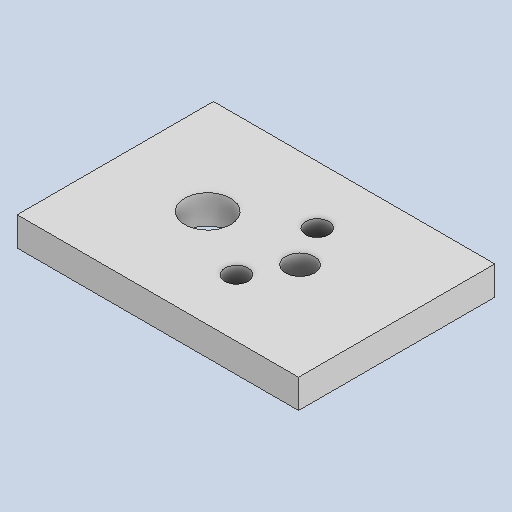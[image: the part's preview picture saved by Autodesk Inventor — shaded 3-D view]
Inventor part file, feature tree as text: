
AUTODESK INVENTOR PART (.ipt)
format: ipt  version: 2025.1 (Build 291241020, 241B)  size: 131,584 bytes
history: native  units: in
note: dims shown in document units (in); Inventor stores cm internally (conversion verified against a paired STEP export)
features: hole x4, sketch x3, extrude x1
ambient origin geometry x8: Origin, YZ Plane, XZ Plane, XY Plane, X Axis, Y Axis, Z Axis, Center Point
bodies: Solid1 (feature_tree)
feature tree (8):
  extrude  "Extrusion1"  Depth=1.7in
  sketch  "Sketch2"  dims[d2=0.25in d3=0.0in d10=0.8375in]
  hole  "Hole1"  [1 undecoded]
  hole  "Hole2"  [1 undecoded]
  hole  "Hole3"  [1 undecoded]
  hole  "Hole4"  [1 undecoded]
  sketch  "Sketch1"  dims[d0=2.4375in d1=1.7in]
  sketch  "Sketch3"  dims[d11=0.85in d14=0.85in d15=0.8in d18=0.5in d19=0.5in d20=0.6in d21=0.6in d22=0.25in d23=0.75in d24=0.375in d25=0.25in d26=0.5635in d27=0.432in d28=0.8108in d29=0.3976in d30=0.75in d31=0.375in d32=0.25in d33=0.5635in d34=1.0in d35=0.8108in d36=0.201in d37=0.75in d38=0.385in d39=0.25in d40=0.5635in d41=1.0in d42=0.8108in d43=0.104in d44=0.276in d45=0.375in d46=0.25in d47=0.5635in d48=0.432in d49=0.8108in d50=0.25in d51=0.25in d52=0.125in]
note: 4 required parameter values undecoded (feature->parameter linkage not recoverable at this tier; creation-order binding heuristic only, values carry confidence <= 0.55)
